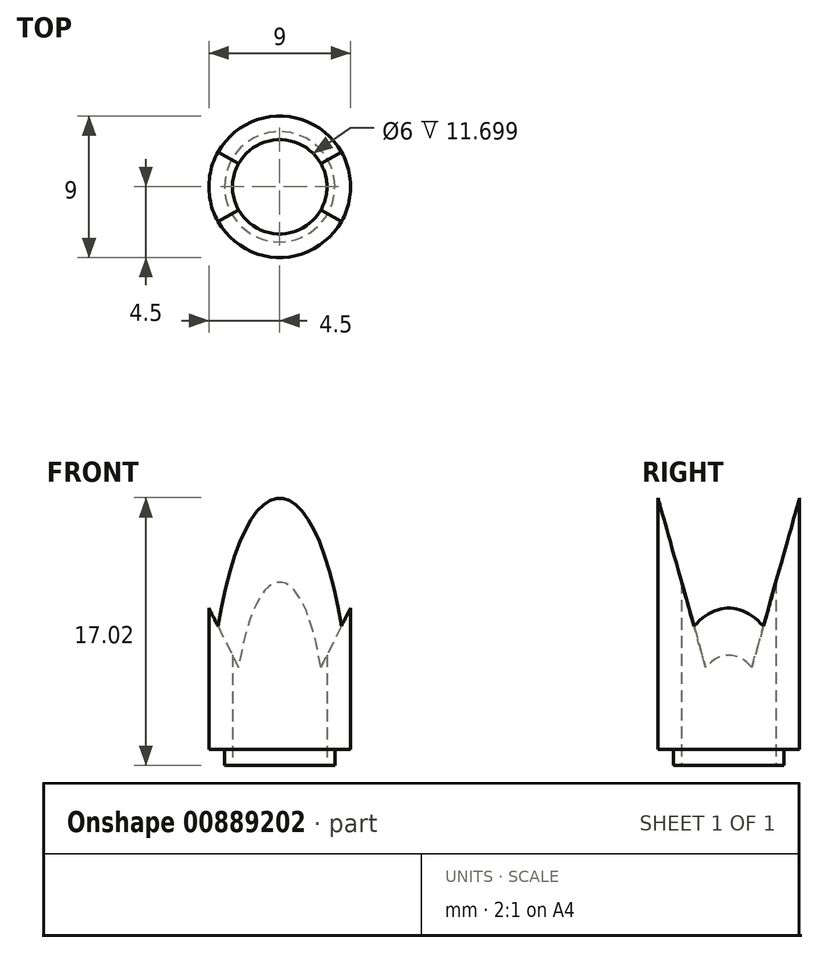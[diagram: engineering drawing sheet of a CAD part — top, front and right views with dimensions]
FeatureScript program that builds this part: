
annotation { "Feature Type Name" : "Feature", "Feature Type Description" : "" }
export const myFeature = defineFeature(function(context is Context, id is Id, definition is map)
    precondition{}
    {
        {
            var Q0;
            Q0=qCreatedBy(makeId("Top.planeOp"),FACE);
            var sketch = newSketch(context, id + "F0", { "sketchPlane" : qUnion([Q0])});
            skCircle(sketch, "E0", {"center": v(0, 0) * mm, "radius": 3 * mm});
            skCircle(sketch, "E1", {"center": v(0, 0) * mm, "radius": 3.5 * mm});
            skSolve(sketch);
        }
        {
            var Q0;
            Q0 = qSketchRegion(id + "F0", true);
            extrude(context, id + "F1", {"entities" : qUnion([Q0]), "depth" : 17.02 * mm, "offsetDistance" : 25.4 * mm});
        }
        {
            var Q0;
            Q0=qCreatedBy(makeId("Top.planeOp"),FACE);
            cPlane(context, id + "F2", {"entities" : qUnion([Q0]), "cplaneType" : CPlaneType.OFFSET, "offset" : 1.02 * mm, "width" : 152.4 * mm, "height" : 152.4 * mm});
        }
        {
            var Q0;
            Q0=qCreatedBy(id+"F2.planeOp",FACE);
            var sketch = newSketch(context, id + "F3", { "sketchPlane" : qUnion([Q0])});
            skPoint(sketch, "E2", {"position": v(0, 0) * mm});
            skCircle(sketch, "E3", {"center": v(0, 0) * mm, "radius": 4.5 * mm});
            skCircle(sketch, "E4", {"center": v(0, 0) * mm, "radius": 3.5 * mm});
            skSolve(sketch);
        }
        {
            var Q0;
            Q0 = qSketchRegion(id + "F3", true);
            var Q1;
            Q1=makeQuery(id+"F1.opExtrude","CAP_FACE",FACE,{"disambiguationData":[OSD([sQuery(id+"F0.wireOp",EDGE,"E0"),sQuery(id+"F0.wireOp",EDGE,"E1")])],"isStart":false});
            extrude(context, id + "F4", {"entities" : qUnion([Q0]), "operationType" : NewBodyOperationType.ADD, "endBound" : BoundingType.UP_TO_SURFACE, "depth" : 25.4 * mm, "endBoundEntityFace" : qUnion([Q1]), "offsetDistance" : 25.4 * mm});
        }
        {
            var Q0;
            Q0=qCreatedBy(id+"F2.planeOp",FACE);
            cPlane(context, id + "F5", {"entities" : qUnion([Q0]), "cplaneType" : CPlaneType.OFFSET, "offset" : 16 * mm, "width" : 152.4 * mm, "height" : 152.4 * mm});
        }
        {
            var Q0;
            Q0=qCreatedBy(id+"F5.planeOp",FACE);
            var sketch = newSketch(context, id + "F6", { "sketchPlane" : qUnion([Q0])});
            skLineSegment(sketch, "E5.bottom", {"start": v(8, 4.5) * mm, "end": v(-8, 4.5) * mm});
            skLineSegment(sketch, "E5.top", {"start": v(8, -4.5) * mm, "end": v(-8, -4.5) * mm});
            skLineSegment(sketch, "E5.left", {"start": v(8, 4.5) * mm, "end": v(8, -4.5) * mm});
            skLineSegment(sketch, "E5.right", {"start": v(-8, 4.5) * mm, "end": v(-8, -4.5) * mm});
            skPoint(sketch, "E5.middle", {"position": v(0, 0) * mm});
            skSolve(sketch);
        }
        {
            var Q1;
            Q1=makeQuery(id+"F6.imprint","IMPRINT",FACE,{"disambiguationData":[TD([[makeQuery(id+"F6.imprint","IMPRINT",EDGE,{"derivedFrom":sQuery(id+"F6.wireOp",EDGE,"E5.bottom")}),1.0]])]});
            var Q2;
            Q2=sQuery(id+"F3.wireOp",VERTEX,"E2");
            loft(context, id + "F7", {"operationType" : NewBodyOperationType.REMOVE, "sheetProfilesArray" : [{ "sheetProfileEntities" : qUnion([Q1]) }, { "sheetProfileEntities" : qUnion([Q2]) }]});
        }
    });
